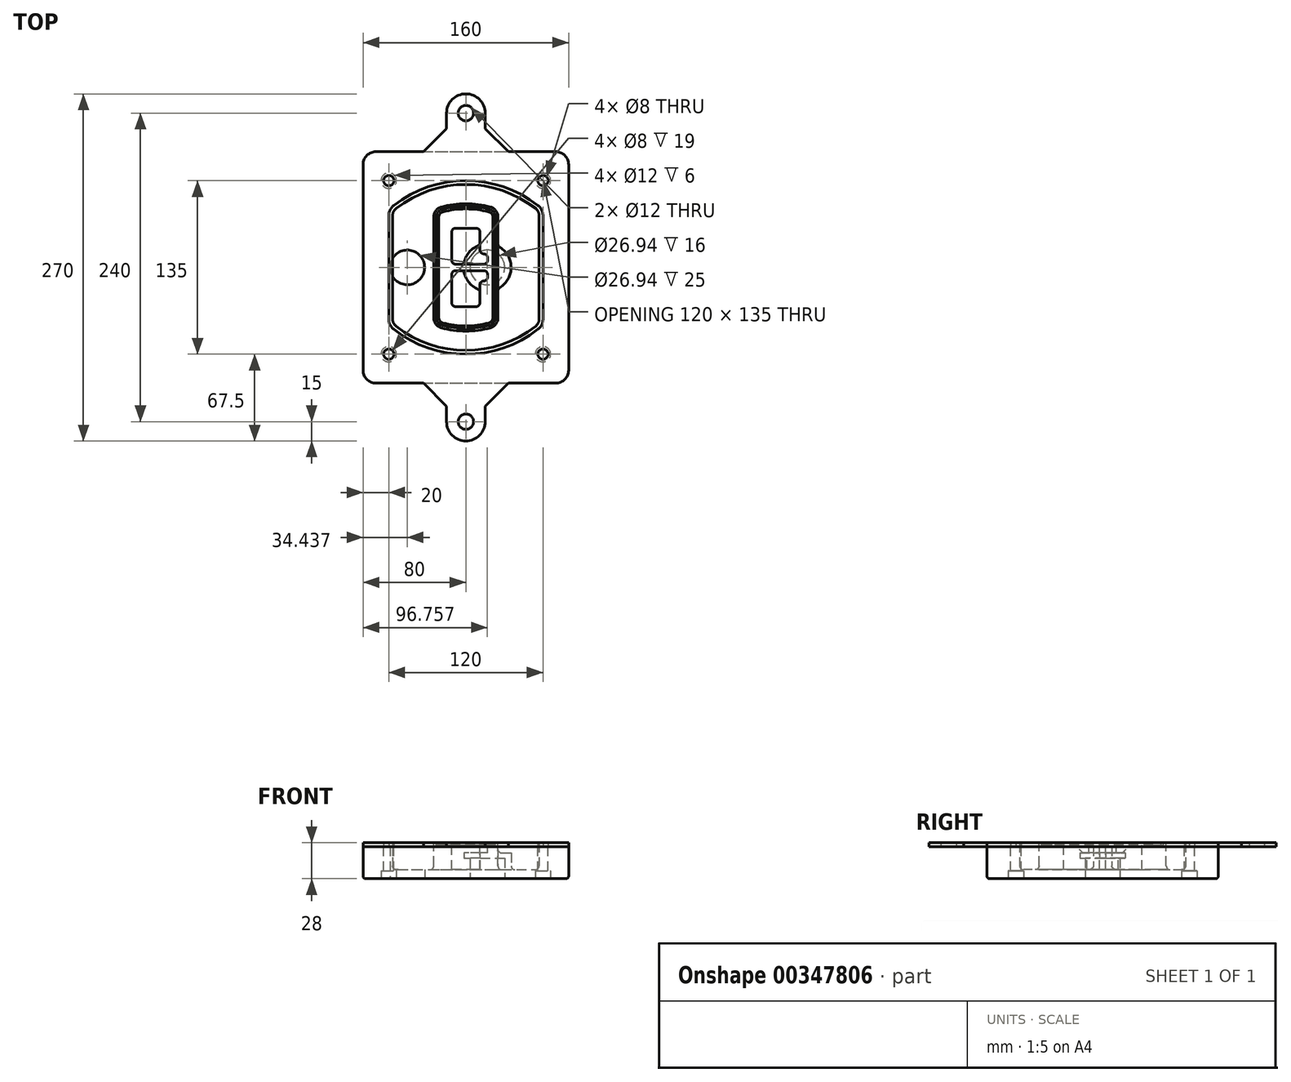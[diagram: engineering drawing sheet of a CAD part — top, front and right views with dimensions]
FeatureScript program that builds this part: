
annotation { "Feature Type Name" : "Feature", "Feature Type Description" : "" }
export const myFeature = defineFeature(function(context is Context, id is Id, definition is map)
    precondition{}
    {
        {
            var Q0;
            Q0=qCreatedBy(makeId("Top.planeOp"),FACE);
            var sketch = newSketch(context, id + "F0", { "sketchPlane" : qUnion([Q0])});
            skPoint(sketch, "E0.rect.middle", {"position": v(0, 0) * mm});
            skLineSegment(sketch, "E1.bottom", {"start": v(-70, -90) * mm, "end": v(70, -90) * mm});
            skLineSegment(sketch, "E1.top", {"start": v(-70, 90) * mm, "end": v(70, 90) * mm});
            skLineSegment(sketch, "E1.left", {"start": v(-80, -80) * mm, "end": v(-80, 80) * mm});
            skLineSegment(sketch, "E1.right", {"start": v(80, -80) * mm, "end": v(80, 80) * mm});
            skLineSegment(sketch, "E2", {"start": v(-80, 90) * mm, "end": v(80, -90) * mm, "construction": true});
            skLineSegment(sketch, "E3", {"start": v(80, 90) * mm, "end": v(-80, -90) * mm, "construction": true});
            skCircle(sketch, "E4", {"center": v(-60, 67.5) * mm, "radius": 4 * mm});
            skCircle(sketch, "E5", {"center": v(60, 67.5) * mm, "radius": 4 * mm});
            skCircle(sketch, "E6", {"center": v(60, -67.5) * mm, "radius": 4 * mm});
            skCircle(sketch, "E7", {"center": v(-60, -67.5) * mm, "radius": 4 * mm});
            skLineSegment(sketch, "E8", {"start": v(-60, 67.5) * mm, "end": v(60, 67.5) * mm, "construction": true});
            skLineSegment(sketch, "E9", {"start": v(60, 67.5) * mm, "end": v(60, -67.5) * mm, "construction": true});
            skLineSegment(sketch, "E10", {"start": v(60, -67.5) * mm, "end": v(-60, -67.5) * mm, "construction": true});
            skLineSegment(sketch, "E11", {"start": v(-60, -67.5) * mm, "end": v(-60, 67.5) * mm, "construction": true});
            skLineSegment(sketch, "E12", {"start": v(-60, 40.3) * mm, "end": v(-60, -40.3) * mm});
            skLineSegment(sketch, "E13", {"start": v(60, 40.3) * mm, "end": v(60, -40.3) * mm});
            skArc(sketch, "E14", {"start": v(56.15, 48.18) * mm, "mid": v(0, 67.5) * mm, "end": v(-56.15, 48.18) * mm});
            skArc(sketch, "E15", {"start": v(-56.15, -48.18) * mm, "mid": v(0, -67.5) * mm, "end": v(56.15, -48.18) * mm});
            skLineSegment(sketch, "E16", {"start": v(-60, 0) * mm, "end": v(60, 0) * mm, "construction": true});
            skPoint(sketch, "E17.visualSharp", {"position": v(-60, -45) * mm});
            skArc(sketch, "E17.filletArc", {"start": v(-60, -40.3) * mm, "mid": v(-58.99, -44.68) * mm, "end": v(-56.15, -48.18) * mm});
            skPoint(sketch, "E18.visualSharp", {"position": v(-60, 45) * mm});
            skArc(sketch, "E18.filletArc", {"start": v(-56.15, 48.18) * mm, "mid": v(-58.99, 44.68) * mm, "end": v(-60, 40.3) * mm});
            skPoint(sketch, "E19.visualSharp", {"position": v(60, 45) * mm});
            skArc(sketch, "E19.filletArc", {"start": v(60, 40.3) * mm, "mid": v(58.99, 44.68) * mm, "end": v(56.15, 48.18) * mm});
            skPoint(sketch, "E20.visualSharp", {"position": v(60, -45) * mm});
            skArc(sketch, "E20.filletArc", {"start": v(56.15, -48.18) * mm, "mid": v(58.99, -44.68) * mm, "end": v(60, -40.3) * mm});
            skPoint(sketch, "E21.visualSharp", {"position": v(-80, 90) * mm});
            skArc(sketch, "E21.filletArc", {"start": v(-70, 90) * mm, "mid": v(-77.07, 87.07) * mm, "end": v(-80, 80) * mm});
            skPoint(sketch, "E22.visualSharp", {"position": v(80, 90) * mm});
            skArc(sketch, "E22.filletArc", {"start": v(80, 80) * mm, "mid": v(77.07, 87.07) * mm, "end": v(70, 90) * mm});
            skPoint(sketch, "E23.visualSharp", {"position": v(80, -90) * mm});
            skArc(sketch, "E23.filletArc", {"start": v(70, -90) * mm, "mid": v(77.07, -87.07) * mm, "end": v(80, -80) * mm});
            skPoint(sketch, "E24.visualSharp", {"position": v(-80, -90) * mm});
            skArc(sketch, "E24.filletArc", {"start": v(-80, -80) * mm, "mid": v(-77.07, -87.07) * mm, "end": v(-70, -90) * mm});
            skArc(sketch, "E25.0", {"start": v(57, 40.3) * mm, "mid": v(56.3, 43.36) * mm, "end": v(54.3, 45.81) * mm});
            skLineSegment(sketch, "E25.1", {"start": v(57, 40.3) * mm, "end": v(57, -40.3) * mm});
            skArc(sketch, "E25.2", {"start": v(54.3, -45.81) * mm, "mid": v(56.3, -43.36) * mm, "end": v(57, -40.3) * mm});
            skArc(sketch, "E25.3", {"start": v(-54.3, -45.81) * mm, "mid": v(0, -64.5) * mm, "end": v(54.3, -45.81) * mm});
            skArc(sketch, "E25.4", {"start": v(-57, -40.3) * mm, "mid": v(-56.3, -43.36) * mm, "end": v(-54.3, -45.81) * mm});
            skArc(sketch, "E25.5", {"start": v(54.3, 45.81) * mm, "mid": v(0, 64.5) * mm, "end": v(-54.3, 45.81) * mm});
            skLineSegment(sketch, "E25.6", {"start": v(-57, 40.3) * mm, "end": v(-57, -40.3) * mm});
            skArc(sketch, "E25.7", {"start": v(-54.3, 45.81) * mm, "mid": v(-56.3, 43.36) * mm, "end": v(-57, 40.3) * mm});
            skArc(sketch, "E26.0", {"start": v(-58.62, 51.33) * mm, "mid": v(-62.58, 46.43) * mm, "end": v(-64, 40.3) * mm});
            skArc(sketch, "E26.1", {"start": v(58.62, 51.33) * mm, "mid": v(0, 71.5) * mm, "end": v(-58.62, 51.33) * mm});
            skArc(sketch, "E26.2", {"start": v(64, 40.3) * mm, "mid": v(62.58, 46.43) * mm, "end": v(58.62, 51.33) * mm});
            skLineSegment(sketch, "E26.3", {"start": v(64, 40.3) * mm, "end": v(64, -40.3) * mm});
            skArc(sketch, "E26.4", {"start": v(58.62, -51.33) * mm, "mid": v(62.58, -46.43) * mm, "end": v(64, -40.3) * mm});
            skLineSegment(sketch, "E26.5", {"start": v(-64, 40.3) * mm, "end": v(-64, -40.3) * mm});
            skArc(sketch, "E26.6", {"start": v(-58.62, -51.33) * mm, "mid": v(0, -71.5) * mm, "end": v(58.62, -51.33) * mm});
            skArc(sketch, "E26.7", {"start": v(-64, -40.3) * mm, "mid": v(-62.58, -46.43) * mm, "end": v(-58.62, -51.33) * mm});
            skSolve(sketch);
        }
        {
            var Q0;
            Q0=makeQuery(id+"F0.imprint","IMPRINT",FACE,{"disambiguationData":[TD([[makeQuery(id+"F0.imprint","IMPRINT",EDGE,{"derivedFrom":sQuery(id+"F0.wireOp",EDGE,"E1.bottom")}),1.0]])]});
            var Q1;
            Q1=makeQuery(id+"F0.imprint","IMPRINT",FACE,{"disambiguationData":[TD([[makeQuery(id+"F0.imprint","IMPRINT",EDGE,{"derivedFrom":sQuery(id+"F0.wireOp",EDGE,"E12")}),1.0]])]});
            var Q2;
            Q2=makeQuery(id+"F0.imprint","IMPRINT",FACE,{"disambiguationData":[TD([[makeQuery(id+"F0.imprint","IMPRINT",EDGE,{"derivedFrom":sQuery(id+"F0.wireOp",EDGE,"E25.0")}),1.0]])]});
            var Q3;
            Q3=makeQuery(id+"F0.imprint","IMPRINT",FACE,{"disambiguationData":[TD([[makeQuery(id+"F0.imprint","IMPRINT",EDGE,{"derivedFrom":sQuery(id+"F0.wireOp",EDGE,"E12")}),-1.0]])]});
            extrude(context, id + "F1", {"entities" : qUnion([Q0, Q1, Q2, Q3]), "oppositeDirection" : true, "depth" : 25 * mm});
        }
        {
            var Q0;
            Q0=makeQuery(id+"F0.imprint","IMPRINT",FACE,{"disambiguationData":[TD([[makeQuery(id+"F0.imprint","IMPRINT",EDGE,{"derivedFrom":sQuery(id+"F0.wireOp",EDGE,"E12")}),1.0]])]});
            extrude(context, id + "F2", {"entities" : qUnion([Q0]), "operationType" : NewBodyOperationType.ADD, "depth" : 3 * mm});
        }
        {
            var Q0;
            Q0=makeQuery(id+"F0.imprint","IMPRINT",FACE,{"disambiguationData":[TD([[makeQuery(id+"F0.imprint","IMPRINT",EDGE,{"derivedFrom":sQuery(id+"F0.wireOp",EDGE,"E25.0")}),1.0]])]});
            extrude(context, id + "F3", {"entities" : qUnion([Q0]), "operationType" : NewBodyOperationType.REMOVE, "oppositeDirection" : true, "depth" : 18 * mm});
        }
        {
            var Q0;
            Q0=makeQuery(id+"F2.opExtrude","CAP_FACE",FACE,{"disambiguationData":[OSD([sQuery(id+"F0.wireOp",EDGE,"E12"),sQuery(id+"F0.wireOp",EDGE,"E13"),sQuery(id+"F0.wireOp",EDGE,"E14"),sQuery(id+"F0.wireOp",EDGE,"E15"),sQuery(id+"F0.wireOp",EDGE,"E17.filletArc"),sQuery(id+"F0.wireOp",EDGE,"E18.filletArc"),sQuery(id+"F0.wireOp",EDGE,"E19.filletArc"),sQuery(id+"F0.wireOp",EDGE,"E20.filletArc"),sQuery(id+"F0.wireOp",EDGE,"E25.0"),sQuery(id+"F0.wireOp",EDGE,"E25.1"),sQuery(id+"F0.wireOp",EDGE,"E25.2"),sQuery(id+"F0.wireOp",EDGE,"E25.3"),sQuery(id+"F0.wireOp",EDGE,"E25.4"),sQuery(id+"F0.wireOp",EDGE,"E25.5"),sQuery(id+"F0.wireOp",EDGE,"E25.6"),sQuery(id+"F0.wireOp",EDGE,"E25.7")])],"isStart":false});
            var sketch = newSketch(context, id + "F4", { "sketchPlane" : qUnion([Q0])});
            skArc(sketch, "E27.0", {"start": v(-19.08, -46.97) * mm, "mid": v(0, -49.5) * mm, "end": v(19.08, -46.97) * mm});
            skArc(sketch, "E28.0", {"start": v(19.08, 46.97) * mm, "mid": v(0, 49.5) * mm, "end": v(-19.08, 46.97) * mm});
            skLineSegment(sketch, "E29", {"start": v(-25, 39.25) * mm, "end": v(-25, -39.25) * mm});
            skLineSegment(sketch, "E30", {"start": v(25, 39.25) * mm, "end": v(25, -39.25) * mm});
            skLineSegment(sketch, "E31", {"start": v(-25, 45.1) * mm, "end": v(25, 45.1) * mm, "construction": true});
            skLineSegment(sketch, "E32", {"start": v(-25, -45.1) * mm, "end": v(25, -45.1) * mm, "construction": true});
            skPoint(sketch, "E33.visualSharp", {"position": v(-25, 45.1) * mm});
            skArc(sketch, "E33.filletArc", {"start": v(-19.08, 46.97) * mm, "mid": v(-23.35, 44.11) * mm, "end": v(-25, 39.25) * mm});
            skPoint(sketch, "E34.visualSharp", {"position": v(25, 45.1) * mm});
            skArc(sketch, "E34.filletArc", {"start": v(25, 39.25) * mm, "mid": v(23.35, 44.11) * mm, "end": v(19.08, 46.97) * mm});
            skPoint(sketch, "E35.visualSharp", {"position": v(25, -45.1) * mm});
            skArc(sketch, "E35.filletArc", {"start": v(19.08, -46.97) * mm, "mid": v(23.35, -44.11) * mm, "end": v(25, -39.25) * mm});
            skPoint(sketch, "E36.visualSharp", {"position": v(-25, -45.1) * mm});
            skArc(sketch, "E36.filletArc", {"start": v(-25, -39.25) * mm, "mid": v(-23.35, -44.11) * mm, "end": v(-19.08, -46.97) * mm});
            skArc(sketch, "E37.0", {"start": v(54.3, 45.81) * mm, "mid": v(0, 64.5) * mm, "end": v(-54.3, 45.81) * mm});
            skArc(sketch, "E37.1", {"start": v(-54.3, 45.81) * mm, "mid": v(-56.3, 43.36) * mm, "end": v(-57, 40.3) * mm});
            skLineSegment(sketch, "E37.2", {"start": v(-57, 40.3) * mm, "end": v(-57, -40.3) * mm});
            skArc(sketch, "E37.3", {"start": v(-57, -40.3) * mm, "mid": v(-56.3, -43.36) * mm, "end": v(-54.3, -45.81) * mm});
            skArc(sketch, "E37.4", {"start": v(-54.3, -45.81) * mm, "mid": v(0, -64.5) * mm, "end": v(54.3, -45.81) * mm});
            skArc(sketch, "E37.5", {"start": v(54.3, -45.81) * mm, "mid": v(56.3, -43.36) * mm, "end": v(57, -40.3) * mm});
            skLineSegment(sketch, "E37.6", {"start": v(57, 40.3) * mm, "end": v(57, -40.3) * mm});
            skArc(sketch, "E37.7", {"start": v(57, 40.3) * mm, "mid": v(56.3, 43.36) * mm, "end": v(54.3, 45.81) * mm});
            skLineSegment(sketch, "E38.0", {"start": v(23, 39.25) * mm, "end": v(23, -39.25) * mm});
            skArc(sketch, "E38.1", {"start": v(18.56, -45.04) * mm, "mid": v(21.76, -42.9) * mm, "end": v(23, -39.25) * mm});
            skArc(sketch, "E38.2", {"start": v(-18.56, -45.04) * mm, "mid": v(0, -47.5) * mm, "end": v(18.56, -45.04) * mm});
            skArc(sketch, "E38.3", {"start": v(-23, -39.25) * mm, "mid": v(-21.76, -42.9) * mm, "end": v(-18.56, -45.04) * mm});
            skLineSegment(sketch, "E38.4", {"start": v(-23, 39.25) * mm, "end": v(-23, -39.25) * mm});
            skArc(sketch, "E38.5", {"start": v(23, 39.25) * mm, "mid": v(21.76, 42.9) * mm, "end": v(18.56, 45.04) * mm});
            skArc(sketch, "E38.6", {"start": v(-18.56, 45.04) * mm, "mid": v(-21.76, 42.9) * mm, "end": v(-23, 39.25) * mm});
            skArc(sketch, "E38.7", {"start": v(18.56, 45.04) * mm, "mid": v(0, 47.5) * mm, "end": v(-18.56, 45.04) * mm});
            skArc(sketch, "E39.0", {"start": v(21, 39.25) * mm, "mid": v(20.18, 41.68) * mm, "end": v(18.04, 43.1) * mm});
            skLineSegment(sketch, "E39.1", {"start": v(21, 39.25) * mm, "end": v(21, -39.25) * mm});
            skArc(sketch, "E39.2", {"start": v(18.04, -43.1) * mm, "mid": v(20.18, -41.68) * mm, "end": v(21, -39.25) * mm});
            skArc(sketch, "E39.3", {"start": v(-18.04, -43.1) * mm, "mid": v(0, -45.5) * mm, "end": v(18.04, -43.1) * mm});
            skArc(sketch, "E39.4", {"start": v(-21, -39.25) * mm, "mid": v(-20.18, -41.68) * mm, "end": v(-18.04, -43.1) * mm});
            skArc(sketch, "E39.5", {"start": v(18.04, 43.1) * mm, "mid": v(0, 45.5) * mm, "end": v(-18.04, 43.1) * mm});
            skLineSegment(sketch, "E39.6", {"start": v(-21, 39.25) * mm, "end": v(-21, -39.25) * mm});
            skArc(sketch, "E39.7", {"start": v(-18.04, 43.1) * mm, "mid": v(-20.18, 41.68) * mm, "end": v(-21, 39.25) * mm});
            skLineSegment(sketch, "E40", {"start": v(-25, 0) * mm, "end": v(25, 0) * mm, "construction": true});
            skLineSegment(sketch, "E41", {"start": v(-11, 5.5) * mm, "end": v(-11, 27.5) * mm});
            skLineSegment(sketch, "E42", {"start": v(-8, 30.5) * mm, "end": v(8, 30.5) * mm});
            skLineSegment(sketch, "E43", {"start": v(11, 27.5) * mm, "end": v(11, 13.5) * mm});
            skLineSegment(sketch, "E44", {"start": v(14, 10.5) * mm, "end": v(14, 10.5) * mm});
            skLineSegment(sketch, "E45", {"start": v(17, 7.5) * mm, "end": v(17, 5.5) * mm});
            skLineSegment(sketch, "E46", {"start": v(14, 2.5) * mm, "end": v(-8, 2.5) * mm});
            skPoint(sketch, "E47.visualSharp", {"position": v(-11, 30.5) * mm});
            skArc(sketch, "E47.filletArc", {"start": v(-8, 30.5) * mm, "mid": v(-10.12, 29.62) * mm, "end": v(-11, 27.5) * mm});
            skPoint(sketch, "E48.visualSharp", {"position": v(11, 30.5) * mm});
            skArc(sketch, "E48.filletArc", {"start": v(11, 27.5) * mm, "mid": v(10.12, 29.62) * mm, "end": v(8, 30.5) * mm});
            skPoint(sketch, "E49.visualSharp", {"position": v(11, 10.5) * mm});
            skArc(sketch, "E49.filletArc", {"start": v(11, 13.5) * mm, "mid": v(11.88, 11.38) * mm, "end": v(14, 10.5) * mm});
            skPoint(sketch, "E50.visualSharp", {"position": v(17, 10.5) * mm});
            skArc(sketch, "E50.filletArc", {"start": v(17, 7.5) * mm, "mid": v(16.12, 9.62) * mm, "end": v(14, 10.5) * mm});
            skPoint(sketch, "E51.visualSharp", {"position": v(17, 2.5) * mm});
            skArc(sketch, "E51.filletArc", {"start": v(14, 2.5) * mm, "mid": v(16.12, 3.38) * mm, "end": v(17, 5.5) * mm});
            skPoint(sketch, "E52.visualSharp", {"position": v(-11, 2.5) * mm});
            skArc(sketch, "E52.filletArc", {"start": v(-11, 5.5) * mm, "mid": v(-10.12, 3.38) * mm, "end": v(-8, 2.5) * mm});
            skLineSegment(sketch, "E53.0.MirrorCS", {"start": v(14, -2.5) * mm, "end": v(-8, -2.5) * mm});
            skArc(sketch, "E54.0.MirrorCS", {"start": v(-11, -5.5) * mm, "mid": v(-10.12, -3.38) * mm, "end": v(-8, -2.5) * mm});
            skLineSegment(sketch, "E55.0.MirrorCS", {"start": v(-11, -5.5) * mm, "end": v(-11, -27.5) * mm});
            skArc(sketch, "E56.0.MirrorCS", {"start": v(-8, -30.5) * mm, "mid": v(-10.12, -29.62) * mm, "end": v(-11, -27.5) * mm});
            skLineSegment(sketch, "E57.0.MirrorCS", {"start": v(-8, -30.5) * mm, "end": v(8, -30.5) * mm});
            skArc(sketch, "E58.0.MirrorCS", {"start": v(11, -27.5) * mm, "mid": v(10.12, -29.62) * mm, "end": v(8, -30.5) * mm});
            skLineSegment(sketch, "E59.0.MirrorCS", {"start": v(11, -27.5) * mm, "end": v(11, -13.5) * mm});
            skArc(sketch, "E60.0.MirrorCS", {"start": v(11, -13.5) * mm, "mid": v(11.88, -11.38) * mm, "end": v(14, -10.5) * mm});
            skArc(sketch, "E61.0.MirrorCS", {"start": v(17, -7.5) * mm, "mid": v(16.12, -9.62) * mm, "end": v(14, -10.5) * mm});
            skLineSegment(sketch, "E62.0.MirrorCS", {"start": v(17, -7.5) * mm, "end": v(17, -5.5) * mm});
            skArc(sketch, "E63.0.MirrorCS", {"start": v(14, -2.5) * mm, "mid": v(16.12, -3.38) * mm, "end": v(17, -5.5) * mm});
            skSolve(sketch);
        }
        {
            var Q0;
            Q0=makeQuery(id+"F4.imprint","IMPRINT",FACE,{"disambiguationData":[TD([[makeQuery(id+"F4.imprint","IMPRINT",EDGE,{"derivedFrom":sQuery(id+"F4.wireOp",EDGE,"E27.0")}),1.0]])]});
            var Q1;
            Q1=makeQuery(id+"F4.imprint","IMPRINT",FACE,{"disambiguationData":[TD([[makeQuery(id+"F4.imprint","IMPRINT",EDGE,{"derivedFrom":sQuery(id+"F4.wireOp",EDGE,"E38.0")}),-1.0]])]});
            var Q2;
            Q2=makeQuery(id+"F4.imprint","IMPRINT",FACE,{"disambiguationData":[TD([[makeQuery(id+"F4.imprint","IMPRINT",EDGE,{"derivedFrom":sQuery(id+"F4.wireOp",EDGE,"E39.0")}),1.0]])]});
            extrude(context, id + "F5", {"entities" : qUnion([Q0, Q1, Q2]), "operationType" : NewBodyOperationType.ADD, "endBound" : BoundingType.UP_TO_NEXT, "oppositeDirection" : true, "depth" : 25 * mm});
        }
        {
            var Q0;
            Q0=makeQuery(id+"F4.imprint","IMPRINT",FACE,{"disambiguationData":[TD([[makeQuery(id+"F4.imprint","IMPRINT",EDGE,{"derivedFrom":sQuery(id+"F4.wireOp",EDGE,"E38.0")}),-1.0]])]});
            extrude(context, id + "F6", {"entities" : qUnion([Q0]), "operationType" : NewBodyOperationType.REMOVE, "oppositeDirection" : true, "depth" : 2 * mm});
        }
        {
            var Q0;
            Q0=makeQuery(id+"F1.opExtrude","CAP_FACE",FACE,{"disambiguationData":[OSD([sQuery(id+"F0.wireOp",EDGE,"E1.bottom"),sQuery(id+"F0.wireOp",EDGE,"E1.top"),sQuery(id+"F0.wireOp",EDGE,"E1.left"),sQuery(id+"F0.wireOp",EDGE,"E1.right"),sQuery(id+"F0.wireOp",EDGE,"E4"),sQuery(id+"F0.wireOp",EDGE,"E5"),sQuery(id+"F0.wireOp",EDGE,"E6"),sQuery(id+"F0.wireOp",EDGE,"E7"),sQuery(id+"F0.wireOp",EDGE,"E21.filletArc"),sQuery(id+"F0.wireOp",EDGE,"E22.filletArc"),sQuery(id+"F0.wireOp",EDGE,"E23.filletArc"),sQuery(id+"F0.wireOp",EDGE,"E24.filletArc")])],"isStart":false});
            var sketch = newSketch(context, id + "F7", { "sketchPlane" : qUnion([Q0])});
            skCircle(sketch, "E64", {"center": v(16.76, 0) * mm, "radius": 13.47 * mm});
            skCircle(sketch, "E65", {"center": v(-45.56, 0) * mm, "radius": 13.47 * mm});
            skLineSegment(sketch, "E66", {"start": v(80, 0) * mm, "end": v(-80, 0) * mm});
            skCircle(sketch, "E67", {"center": v(16.76, 0) * mm, "radius": 18.47 * mm});
            skCircle(sketch, "E68", {"center": v(60, -67.5) * mm, "radius": 6 * mm});
            skCircle(sketch, "E69", {"center": v(-60, -67.5) * mm, "radius": 6 * mm});
            skCircle(sketch, "E70", {"center": v(-60, 67.5) * mm, "radius": 6 * mm});
            skCircle(sketch, "E71", {"center": v(60, 67.5) * mm, "radius": 6 * mm});
            skSolve(sketch);
        }
        {
            var Q0;
            {var subQ1=sQuery(id+"F7.wireOp",EDGE,"E66");var subQ4=sQuery(id+"F7.wireOp",EDGE,"E64");var subQ6=makeQuery(id+"F7.imprint","INTERSECT",VERTEX,{"disambiguationData":[OD(0.0)],"derivedFrom":[subQ4,subQ1]});Q0=makeQuery(id+"F7.imprint","IMPRINT",FACE,{"disambiguationData":[TD([[makeQuery(id+"F7.imprint","IMPRINT",EDGE,{"disambiguationData":[TD([[subQ6,-1.0]])],"derivedFrom":subQ4}),-1.0]])]});}
            var Q1;
            {var subQ0=sQuery(id+"F7.wireOp",EDGE,"E66");var subQ1=sQuery(id+"F7.wireOp",EDGE,"E64");var subQ3=makeQuery(id+"F7.imprint","INTERSECT",VERTEX,{"disambiguationData":[OD(0.0)],"derivedFrom":[subQ1,subQ0]});Q1=makeQuery(id+"F7.imprint","IMPRINT",FACE,{"disambiguationData":[TD([[makeQuery(id+"F7.imprint","IMPRINT",EDGE,{"disambiguationData":[TD([[subQ3,-1.0]])],"derivedFrom":subQ1}),1.0]])]});}
            var Q2;
            {var subQ0=sQuery(id+"F7.wireOp",EDGE,"E66");var subQ1=sQuery(id+"F7.wireOp",EDGE,"E64");var subQ3=makeQuery(id+"F7.imprint","INTERSECT",VERTEX,{"disambiguationData":[OD(0.0)],"derivedFrom":[subQ1,subQ0]});Q2=makeQuery(id+"F7.imprint","IMPRINT",FACE,{"disambiguationData":[TD([[makeQuery(id+"F7.imprint","IMPRINT",EDGE,{"disambiguationData":[TD([[subQ3,1.0]])],"derivedFrom":subQ1}),1.0]])]});}
            var Q3;
            {var subQ1=sQuery(id+"F7.wireOp",EDGE,"E66");var subQ4=sQuery(id+"F7.wireOp",EDGE,"E64");var subQ6=makeQuery(id+"F7.imprint","INTERSECT",VERTEX,{"disambiguationData":[OD(0.0)],"derivedFrom":[subQ4,subQ1]});Q3=makeQuery(id+"F7.imprint","IMPRINT",FACE,{"disambiguationData":[TD([[makeQuery(id+"F7.imprint","IMPRINT",EDGE,{"disambiguationData":[TD([[subQ6,1.0]])],"derivedFrom":subQ4}),-1.0]])]});}
            extrude(context, id + "F8", {"entities" : qUnion([Q0, Q1, Q2, Q3]), "operationType" : NewBodyOperationType.ADD, "oppositeDirection" : true, "depth" : 20 * mm});
        }
        {
            var Q0;
            {var subQ0=sQuery(id+"F7.wireOp",EDGE,"E66");var subQ1=sQuery(id+"F7.wireOp",EDGE,"E64");var subQ3=makeQuery(id+"F7.imprint","INTERSECT",VERTEX,{"disambiguationData":[OD(0.0)],"derivedFrom":[subQ1,subQ0]});Q0=makeQuery(id+"F7.imprint","IMPRINT",FACE,{"disambiguationData":[TD([[makeQuery(id+"F7.imprint","IMPRINT",EDGE,{"disambiguationData":[TD([[subQ3,-1.0]])],"derivedFrom":subQ1}),1.0]])]});}
            var Q1;
            {var subQ0=sQuery(id+"F7.wireOp",EDGE,"E66");var subQ1=sQuery(id+"F7.wireOp",EDGE,"E64");var subQ3=makeQuery(id+"F7.imprint","INTERSECT",VERTEX,{"disambiguationData":[OD(0.0)],"derivedFrom":[subQ1,subQ0]});Q1=makeQuery(id+"F7.imprint","IMPRINT",FACE,{"disambiguationData":[TD([[makeQuery(id+"F7.imprint","IMPRINT",EDGE,{"disambiguationData":[TD([[subQ3,1.0]])],"derivedFrom":subQ1}),1.0]])]});}
            extrude(context, id + "F9", {"entities" : qUnion([Q0, Q1]), "operationType" : NewBodyOperationType.REMOVE, "oppositeDirection" : true, "depth" : 16 * mm});
        }
        {
            var Q0;
            {var subQ0=sQuery(id+"F7.wireOp",EDGE,"E66");var subQ1=sQuery(id+"F7.wireOp",EDGE,"E65");var subQ3=makeQuery(id+"F7.imprint","INTERSECT",VERTEX,{"disambiguationData":[OD(0.0)],"derivedFrom":[subQ1,subQ0]});Q0=makeQuery(id+"F7.imprint","IMPRINT",FACE,{"disambiguationData":[TD([[makeQuery(id+"F7.imprint","IMPRINT",EDGE,{"disambiguationData":[TD([[subQ3,-1.0]])],"derivedFrom":subQ1}),1.0]])]});}
            var Q1;
            {var subQ0=sQuery(id+"F7.wireOp",EDGE,"E66");var subQ1=sQuery(id+"F7.wireOp",EDGE,"E65");var subQ3=makeQuery(id+"F7.imprint","INTERSECT",VERTEX,{"disambiguationData":[OD(0.0)],"derivedFrom":[subQ1,subQ0]});Q1=makeQuery(id+"F7.imprint","IMPRINT",FACE,{"disambiguationData":[TD([[makeQuery(id+"F7.imprint","IMPRINT",EDGE,{"disambiguationData":[TD([[subQ3,1.0]])],"derivedFrom":subQ1}),1.0]])]});}
            extrude(context, id + "F10", {"entities" : qUnion([Q0, Q1]), "operationType" : NewBodyOperationType.REMOVE, "oppositeDirection" : true, "depth" : 25 * mm});
        }
        {
            var Q0;
            Q0=makeQuery(id+"F7.imprint","IMPRINT",FACE,{"disambiguationData":[TD([[makeQuery(id+"F7.imprint","IMPRINT",EDGE,{"derivedFrom":sQuery(id+"F7.wireOp",EDGE,"E68")}),1.0]])]});
            var Q1;
            Q1=makeQuery(id+"F7.imprint","IMPRINT",FACE,{"disambiguationData":[TD([[makeQuery(id+"F7.imprint","IMPRINT",EDGE,{"derivedFrom":makeQuery(id+"F1.opExtrude","CAP_EDGE",EDGE,{"disambiguationData":[OSD([sQuery(id+"F0.wireOp",EDGE,"E5")])],"isStart":false})}),-1.0]])]});
            var Q2;
            Q2=makeQuery(id+"F7.imprint","IMPRINT",FACE,{"disambiguationData":[TD([[makeQuery(id+"F7.imprint","IMPRINT",EDGE,{"derivedFrom":sQuery(id+"F7.wireOp",EDGE,"E69")}),1.0]])]});
            var Q3;
            Q3=makeQuery(id+"F7.imprint","IMPRINT",FACE,{"disambiguationData":[TD([[makeQuery(id+"F7.imprint","IMPRINT",EDGE,{"derivedFrom":makeQuery(id+"F1.opExtrude","CAP_EDGE",EDGE,{"disambiguationData":[OSD([sQuery(id+"F0.wireOp",EDGE,"E4")])],"isStart":false})}),-1.0]])]});
            var Q4;
            Q4=makeQuery(id+"F7.imprint","IMPRINT",FACE,{"disambiguationData":[TD([[makeQuery(id+"F7.imprint","IMPRINT",EDGE,{"derivedFrom":sQuery(id+"F7.wireOp",EDGE,"E70")}),1.0]])]});
            var Q5;
            Q5=makeQuery(id+"F7.imprint","IMPRINT",FACE,{"disambiguationData":[TD([[makeQuery(id+"F7.imprint","IMPRINT",EDGE,{"derivedFrom":makeQuery(id+"F1.opExtrude","CAP_EDGE",EDGE,{"disambiguationData":[OSD([sQuery(id+"F0.wireOp",EDGE,"E7")])],"isStart":false})}),-1.0]])]});
            var Q6;
            Q6=makeQuery(id+"F7.imprint","IMPRINT",FACE,{"disambiguationData":[TD([[makeQuery(id+"F7.imprint","IMPRINT",EDGE,{"derivedFrom":sQuery(id+"F7.wireOp",EDGE,"E71")}),1.0]])]});
            var Q7;
            Q7=makeQuery(id+"F7.imprint","IMPRINT",FACE,{"disambiguationData":[TD([[makeQuery(id+"F7.imprint","IMPRINT",EDGE,{"derivedFrom":makeQuery(id+"F1.opExtrude","CAP_EDGE",EDGE,{"disambiguationData":[OSD([sQuery(id+"F0.wireOp",EDGE,"E6")])],"isStart":false})}),-1.0]])]});
            extrude(context, id + "F11", {"entities" : qUnion([Q0, Q1, Q2, Q3, Q4, Q5, Q6, Q7]), "operationType" : NewBodyOperationType.REMOVE, "oppositeDirection" : true, "depth" : 6 * mm});
        }
        {
            var Q0;
            Q0=makeQuery(id+"F9.boolean.opBoolean","COPY",FACE,{"derivedFrom":makeQuery(id+"F9.opExtrude","CAP_FACE",FACE,{"disambiguationData":[OSD([sQuery(id+"F7.wireOp",EDGE,"E64")])],"isStart":false})});
            var sketch = newSketch(context, id + "F12", { "sketchPlane" : qUnion([Q0])});
            skArc(sketch, "E72.0", {"start": v(11, 17.55) * mm, "mid": v(2.57, 11.82) * mm, "end": v(-1.54, 2.5) * mm});
            skArc(sketch, "E72.1", {"start": v(-1.54, -2.5) * mm, "mid": v(2.57, -11.82) * mm, "end": v(11, -17.55) * mm});
            skLineSegment(sketch, "E73", {"start": v(-1.54, -2.5) * mm, "end": v(14, -2.5) * mm});
            skLineSegment(sketch, "E74.0", {"start": v(14, 2.5) * mm, "end": v(-1.54, 2.5) * mm});
            skArc(sketch, "E74.1", {"start": v(14, 2.5) * mm, "mid": v(16.12, 3.38) * mm, "end": v(17, 5.5) * mm});
            skLineSegment(sketch, "E74.2", {"start": v(17, 7.5) * mm, "end": v(17, 5.5) * mm});
            skArc(sketch, "E74.3", {"start": v(17, 7.5) * mm, "mid": v(16.12, 9.62) * mm, "end": v(14, 10.5) * mm});
            skArc(sketch, "E74.4", {"start": v(11, 13.5) * mm, "mid": v(11.88, 11.38) * mm, "end": v(14, 10.5) * mm});
            skLineSegment(sketch, "E74.5", {"start": v(11, 17.55) * mm, "end": v(11, 13.5) * mm});
            skLineSegment(sketch, "E74.7", {"start": v(14, -2.5) * mm, "end": v(-1.54, -2.5) * mm});
            skArc(sketch, "E74.8", {"start": v(14, -2.5) * mm, "mid": v(16.12, -3.38) * mm, "end": v(17, -5.5) * mm});
            skLineSegment(sketch, "E74.9", {"start": v(17, -7.5) * mm, "end": v(17, -5.5) * mm});
            skArc(sketch, "E74.10", {"start": v(17, -7.5) * mm, "mid": v(16.12, -9.62) * mm, "end": v(14, -10.5) * mm});
            skArc(sketch, "E74.11", {"start": v(11, -13.5) * mm, "mid": v(11.88, -11.38) * mm, "end": v(14, -10.5) * mm});
            skLineSegment(sketch, "E74.12", {"start": v(11, -17.55) * mm, "end": v(11, -13.5) * mm});
            skPoint(sketch, "E75.orphan", {"position": v(11, -27.5) * mm});
            skPoint(sketch, "E76.orphan", {"position": v(-8, -2.5) * mm});
            skPoint(sketch, "E77.orphan", {"position": v(-8, 2.5) * mm});
            skPoint(sketch, "E78.orphan", {"position": v(11, 27.5) * mm});
            skSolve(sketch);
        }
        {
            var Q0;
            {var subQ7=sQuery(id+"F12.wireOp",EDGE,"E72.0");var subQ14=sQuery(id+"F12.wireOp",EDGE,"E72.1");var subQ16=sQuery(id+"F12.wireOp",EDGE,"E74.1");var subQ18=sQuery(id+"F12.wireOp",EDGE,"E74.8");Q0=qUnion([makeQuery(id+"F12.imprint","IMPRINT",FACE,{"disambiguationData":[TD([[makeQuery(id+"F12.imprint","IMPRINT",EDGE,{"derivedFrom":subQ7}),1.0]])]}),makeQuery(id+"F12.imprint","IMPRINT",FACE,{"disambiguationData":[TD([[makeQuery(id+"F12.imprint","IMPRINT",EDGE,{"derivedFrom":subQ14}),1.0]])]}),makeQuery(id+"F12.imprint","IMPRINT",FACE,{"disambiguationData":[TD([[makeQuery(id+"F12.imprint","IMPRINT",EDGE,{"derivedFrom":subQ16}),1.0]])]}),makeQuery(id+"F12.imprint","IMPRINT",FACE,{"disambiguationData":[TD([[makeQuery(id+"F12.imprint","IMPRINT",EDGE,{"derivedFrom":subQ18}),-1.0]])]})]);}
            var Q1;
            Q1=makeQuery(id+"F5.boolean.opBoolean","SPLIT",FACE,{"disambiguationData":[TD([makeQuery(id+"F5.opExtrude","SWEPT_FACE",FACE,{"disambiguationData":[OSD([sQuery(id+"F4.wireOp",EDGE,"E41")])]})])],"derivedFrom":makeQuery(id+"F3.boolean.opBoolean","COPY",FACE,{"derivedFrom":makeQuery(id+"F3.opExtrude","CAP_FACE",FACE,{"disambiguationData":[OSD([sQuery(id+"F0.wireOp",EDGE,"E25.0"),sQuery(id+"F0.wireOp",EDGE,"E25.1"),sQuery(id+"F0.wireOp",EDGE,"E25.2"),sQuery(id+"F0.wireOp",EDGE,"E25.3"),sQuery(id+"F0.wireOp",EDGE,"E25.4"),sQuery(id+"F0.wireOp",EDGE,"E25.5"),sQuery(id+"F0.wireOp",EDGE,"E25.6"),sQuery(id+"F0.wireOp",EDGE,"E25.7")])],"isStart":false})})});
            extrude(context, id + "F13", {"entities" : qUnion([Q0]), "operationType" : NewBodyOperationType.REMOVE, "endBound" : BoundingType.UP_TO_SURFACE, "endBoundEntityFace" : qUnion([Q1]), "depth" : 25 * mm});
        }
        {
            var Q0;
            Q0=makeQuery(id+"F3.boolean.opBoolean","COPY",EDGE,{"derivedFrom":makeQuery(id+"F3.opExtrude","CAP_EDGE",EDGE,{"disambiguationData":[OSD([sQuery(id+"F0.wireOp",EDGE,"E25.6")])],"isStart":false})});
            var Q1;
            Q1=makeQuery(id+"F8.boolean.opBoolean","INTERSECT",EDGE,{"derivedFrom":[makeQuery(id+"F5.opExtrude","SWEPT_FACE",FACE,{"disambiguationData":[OSD([sQuery(id+"F4.wireOp",EDGE,"E30")])]}),makeQuery(id+"F8.opExtrude","CAP_FACE",FACE,{"disambiguationData":[OSD([sQuery(id+"F7.wireOp",EDGE,"E67")])],"isStart":false})]});
            var Q2;
            Q2=makeQuery(id+"F8.boolean.opBoolean","INTERSECT",EDGE,{"disambiguationData":[OD(1.0)],"derivedFrom":[makeQuery(id+"F5.opExtrude","SWEPT_FACE",FACE,{"disambiguationData":[OSD([sQuery(id+"F4.wireOp",EDGE,"E30")])]}),makeQuery(id+"F8.opExtrude","SWEPT_FACE",FACE,{"disambiguationData":[OSD([sQuery(id+"F7.wireOp",EDGE,"E67")])]})]});
            var Q3;
            {var subQ0=sQuery(id+"F4.wireOp",EDGE,"E30");Q3=makeQuery(id+"F8.boolean.opBoolean","SPLIT",EDGE,{"disambiguationData":[TD([makeQuery(id+"F5.opExtrude","SWEPT_FACE",FACE,{"disambiguationData":[OSD([sQuery(id+"F4.wireOp",EDGE,"E35.filletArc")])]})])],"derivedFrom":makeQuery(id+"F5.opExtrude","CAP_EDGE",EDGE,{"disambiguationData":[OSD([subQ0])],"isStart":false})});}
            var Q4;
            {var subQ0=sQuery(id+"F0.wireOp",EDGE,"E25.7");var subQ1=sQuery(id+"F0.wireOp",EDGE,"E25.1");var subQ2=sQuery(id+"F0.wireOp",EDGE,"E25.6");var subQ3=sQuery(id+"F0.wireOp",EDGE,"E25.5");var subQ4=sQuery(id+"F0.wireOp",EDGE,"E25.4");var subQ5=sQuery(id+"F0.wireOp",EDGE,"E25.0");var subQ6=sQuery(id+"F0.wireOp",EDGE,"E25.2");var subQ7=sQuery(id+"F0.wireOp",EDGE,"E25.3");Q4=makeQuery(id+"F8.boolean.opBoolean","INTERSECT",EDGE,{"derivedFrom":[makeQuery(id+"F5.boolean.opBoolean","SPLIT",FACE,{"disambiguationData":[TD([makeQuery(id+"F2.opExtrude","SWEPT_FACE",FACE,{"disambiguationData":[OSD([subQ5])]})])],"derivedFrom":makeQuery(id+"F3.boolean.opBoolean","COPY",FACE,{"derivedFrom":makeQuery(id+"F3.opExtrude","CAP_FACE",FACE,{"disambiguationData":[OSD([subQ5,subQ1,subQ6,subQ7,subQ4,subQ3,subQ2,subQ0])],"isStart":false})})}),makeQuery(id+"F8.opExtrude","SWEPT_FACE",FACE,{"disambiguationData":[OSD([sQuery(id+"F7.wireOp",EDGE,"E67")])]})]});}
            var Q5;
            Q5=makeQuery(id+"F8.boolean.opBoolean","INTERSECT",EDGE,{"disambiguationData":[OD(0.0)],"derivedFrom":[makeQuery(id+"F5.opExtrude","SWEPT_FACE",FACE,{"disambiguationData":[OSD([sQuery(id+"F4.wireOp",EDGE,"E30")])]}),makeQuery(id+"F8.opExtrude","SWEPT_FACE",FACE,{"disambiguationData":[OSD([sQuery(id+"F7.wireOp",EDGE,"E67")])]})]});
            fillet(context, id + "F14", {"entities" : qUnion([Q0, Q1, Q2, Q3, Q4, Q5]), "radius" : 3 * mm, "tangentPropagation" : true, "allowEdgeOverflow" : false});
        }
        {
            var Q0;
            Q0=makeQuery(id+"F1.opExtrude","CAP_EDGE",EDGE,{"disambiguationData":[OSD([sQuery(id+"F0.wireOp",EDGE,"E1.bottom")])],"isStart":false});
            fillet(context, id + "F15", {"entities" : qUnion([Q0]), "radius" : 2 * mm, "tangentPropagation" : true, "allowEdgeOverflow" : false});
        }
        {
            var Q0;
            {var subQ0=sQuery(id+"F0.wireOp",EDGE,"E21.filletArc");var subQ1=sQuery(id+"F0.wireOp",EDGE,"E7");var subQ2=sQuery(id+"F0.wireOp",EDGE,"E6");var subQ3=sQuery(id+"F0.wireOp",EDGE,"E5");var subQ4=sQuery(id+"F0.wireOp",EDGE,"E4");var subQ5=sQuery(id+"F0.wireOp",EDGE,"E22.filletArc");var subQ6=sQuery(id+"F0.wireOp",EDGE,"E1.bottom");var subQ7=sQuery(id+"F0.wireOp",EDGE,"E1.right");var subQ8=sQuery(id+"F0.wireOp",EDGE,"E1.top");var subQ9=sQuery(id+"F0.wireOp",EDGE,"E1.left");var subQ10=sQuery(id+"F0.wireOp",EDGE,"E23.filletArc");var subQ11=sQuery(id+"F0.wireOp",EDGE,"E24.filletArc");Q0=makeQuery(id+"F2.boolean.opBoolean","SPLIT",FACE,{"disambiguationData":[TD([makeQuery(id+"F1.opExtrude","SWEPT_FACE",FACE,{"disambiguationData":[OSD([subQ6])]})])],"derivedFrom":makeQuery(id+"F1.opExtrude","CAP_FACE",FACE,{"disambiguationData":[OSD([subQ6,subQ8,subQ9,subQ7,subQ4,subQ3,subQ2,subQ1,subQ0,subQ5,subQ10,subQ11])],"isStart":true})});}
            var sketch = newSketch(context, id + "F16", { "sketchPlane" : qUnion([Q0])});
            skLineSegment(sketch, "E79", {"start": v(0, 90) * mm, "end": v(0, 120) * mm, "construction": true});
            skCircle(sketch, "E80", {"center": v(0, 120) * mm, "radius": 6 * mm});
            skArc(sketch, "E81", {"start": v(15, 120) * mm, "mid": v(0, 135) * mm, "end": v(-15, 120) * mm});
            skLineSegment(sketch, "E82", {"start": v(15, 120) * mm, "end": v(15, 108) * mm});
            skLineSegment(sketch, "E83", {"start": v(-15, 120) * mm, "end": v(-15, 108) * mm});
            skLineSegment(sketch, "E84", {"start": v(-15, 108) * mm, "end": v(-33, 90) * mm});
            skLineSegment(sketch, "E85", {"start": v(15, 108) * mm, "end": v(33, 90) * mm});
            skLineSegment(sketch, "E86", {"start": v(-80, 0) * mm, "end": v(80, 0) * mm, "construction": true});
            skLineSegment(sketch, "E87.MirrorCS", {"start": v(15, -108) * mm, "end": v(33, -90) * mm});
            skLineSegment(sketch, "E88.MirrorCS", {"start": v(15, -120) * mm, "end": v(15, -108) * mm});
            skArc(sketch, "E89.MirrorCS", {"start": v(15, -120) * mm, "mid": v(0, -135) * mm, "end": v(-15, -120) * mm});
            skLineSegment(sketch, "E90.MirrorCS", {"start": v(-15, -120) * mm, "end": v(-15, -108) * mm});
            skLineSegment(sketch, "E91.MirrorCS", {"start": v(-15, -108) * mm, "end": v(-33, -90) * mm});
            skLineSegment(sketch, "E92.MirrorCS", {"start": v(0, -90) * mm, "end": v(0, -120) * mm, "construction": true});
            skCircle(sketch, "E93.MirrorC", {"center": v(0, -120) * mm, "radius": 6 * mm});
            skSolve(sketch);
        }
        {
            var Q0;
            {var subQ0=sQuery(id+"F16.wireOp",EDGE,"E87.MirrorCS");Q0=makeQuery(id+"F16.imprint","IMPRINT",FACE,{"disambiguationData":[TD([[makeQuery(id+"F16.imprint","IMPRINT",EDGE,{"derivedFrom":subQ0}),1.0]])]});}
            var Q1;
            Q1=makeQuery(id+"F16.imprint","IMPRINT",FACE,{"disambiguationData":[TD([[makeQuery(id+"F16.imprint","IMPRINT",EDGE,{"derivedFrom":makeQuery(id+"F1.opExtrude","CAP_EDGE",EDGE,{"disambiguationData":[OSD([sQuery(id+"F0.wireOp",EDGE,"E1.left")])],"isStart":true})}),-1.0]])]});
            var Q2;
            Q2=makeQuery(id+"F16.imprint","IMPRINT",FACE,{"disambiguationData":[TD([[makeQuery(id+"F16.imprint","IMPRINT",EDGE,{"derivedFrom":sQuery(id+"F16.wireOp",EDGE,"E80")}),-1.0]])]});
            var Q3;
            Q3=makeQuery(id+"F2.opExtrude","CAP_FACE",FACE,{"disambiguationData":[OSD([sQuery(id+"F0.wireOp",EDGE,"E12"),sQuery(id+"F0.wireOp",EDGE,"E13"),sQuery(id+"F0.wireOp",EDGE,"E14"),sQuery(id+"F0.wireOp",EDGE,"E15"),sQuery(id+"F0.wireOp",EDGE,"E17.filletArc"),sQuery(id+"F0.wireOp",EDGE,"E18.filletArc"),sQuery(id+"F0.wireOp",EDGE,"E19.filletArc"),sQuery(id+"F0.wireOp",EDGE,"E20.filletArc"),sQuery(id+"F0.wireOp",EDGE,"E25.0"),sQuery(id+"F0.wireOp",EDGE,"E25.1"),sQuery(id+"F0.wireOp",EDGE,"E25.2"),sQuery(id+"F0.wireOp",EDGE,"E25.3"),sQuery(id+"F0.wireOp",EDGE,"E25.4"),sQuery(id+"F0.wireOp",EDGE,"E25.5"),sQuery(id+"F0.wireOp",EDGE,"E25.6"),sQuery(id+"F0.wireOp",EDGE,"E25.7")])],"isStart":false});
            extrude(context, id + "F17", {"entities" : qUnion([Q0, Q1, Q2]), "endBound" : BoundingType.UP_TO_SURFACE, "endBoundEntityFace" : qUnion([Q3]), "depth" : 25 * mm});
        }
    });
